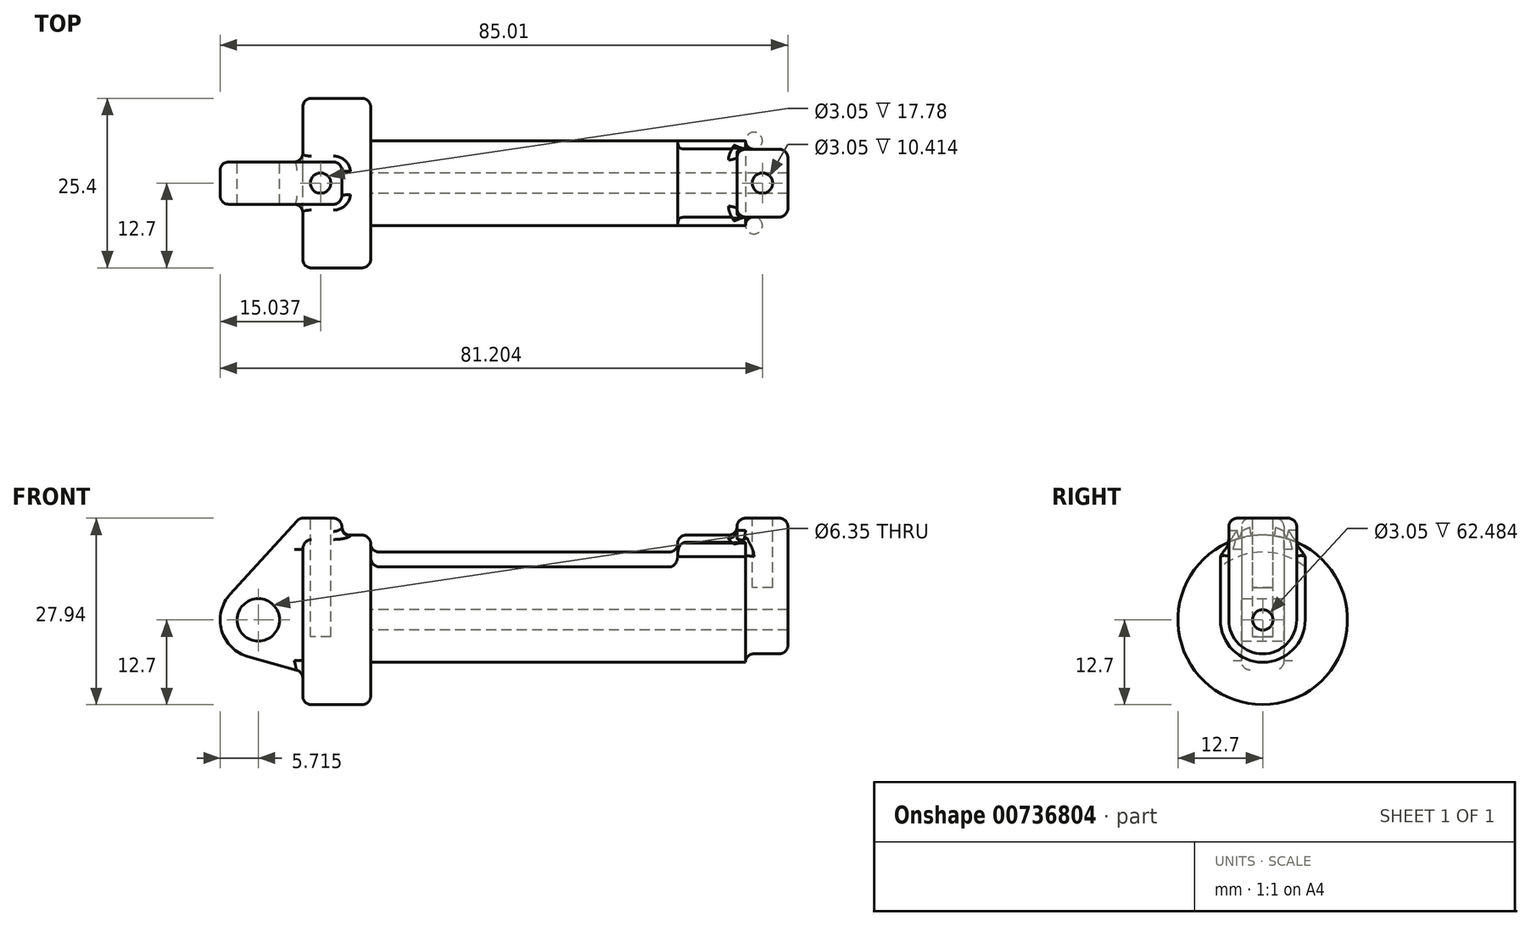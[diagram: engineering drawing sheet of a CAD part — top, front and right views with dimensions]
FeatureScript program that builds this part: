
annotation { "Feature Type Name" : "Feature", "Feature Type Description" : "" }
export const myFeature = defineFeature(function(context is Context, id is Id, definition is map)
    precondition{}
    {
        {
            var Q0;
            Q0=qCreatedBy(makeId("Front.planeOp"),FACE);
            var sketch = newSketch(context, id + "F0", { "sketchPlane" : qUnion([Q0])});
            skLineSegment(sketch, "E0", {"start": v(0, 0) * mm, "end": v(0, 12.7) * mm});
            skLineSegment(sketch, "E1", {"start": v(0, 12.7) * mm, "end": v(10.16, 12.7) * mm});
            skLineSegment(sketch, "E2", {"start": v(10.16, 12.7) * mm, "end": v(10.16, 10.16) * mm});
            skLineSegment(sketch, "E3", {"start": v(10.16, 10.16) * mm, "end": v(56.13, 10.16) * mm});
            skLineSegment(sketch, "E4", {"start": v(56.13, 10.16) * mm, "end": v(56.13, 12.7) * mm});
            skLineSegment(sketch, "E5", {"start": v(56.13, 12.7) * mm, "end": v(66.3, 12.7) * mm});
            skLineSegment(sketch, "E6", {"start": v(66.3, 12.7) * mm, "end": v(66.3, 0) * mm});
            skLineSegment(sketch, "E7", {"start": v(66.3, 0) * mm, "end": v(0, 0) * mm});
            skLineSegment(sketch, "E8", {"start": v(5.84, 15.24) * mm, "end": v(-0.5, 15.24) * mm});
            skLineSegment(sketch, "E9", {"start": v(-0.5, 15.24) * mm, "end": v(-10.88, 3.85) * mm});
            skLineSegment(sketch, "E10", {"start": v(0, 0) * mm, "end": v(-6.65, 0) * mm});
            skCircle(sketch, "E11", {"center": v(-6.65, 0) * mm, "radius": 5.72 * mm});
            skCircle(sketch, "E12", {"center": v(-6.65, 0) * mm, "radius": 3.18 * mm});
            skLineSegment(sketch, "E13", {"start": v(5.84, 15.24) * mm, "end": v(5.84, -9.4) * mm});
            skLineSegment(sketch, "E14", {"start": v(5.84, -9.4) * mm, "end": v(-8.18, -5.5) * mm});
            skSolve(sketch);
        }
        {
            var Q0;
            {var subQ0=sQuery(id+"F0.wireOp",EDGE,"E2");Q0=makeQuery(id+"F0.imprint","IMPRINT",FACE,{"disambiguationData":[TD([[makeQuery(id+"F0.imprint","IMPRINT",EDGE,{"derivedFrom":subQ0}),-1.0]])]});}
            var Q1;
            {var subQ0=sQuery(id+"F0.wireOp",EDGE,"E0");Q1=makeQuery(id+"F0.imprint","IMPRINT",FACE,{"disambiguationData":[TD([[makeQuery(id+"F0.imprint","IMPRINT",EDGE,{"derivedFrom":subQ0}),-1.0]])]});}
            var Q2;
            Q2=sQuery(id+"F0.wireOp",EDGE,"E7");
            revolve(context, id + "F1", {"surfaceOperationType" : NewSurfaceOperationType.NEW, "entities" : qUnion([Q0, Q1]), "axis" : qUnion([Q2]), "revolveType" : RevolveType.FULL});
        }
        {
            var Q0;
            {var subQ1=sQuery(id+"F0.wireOp",EDGE,"E0");Q0=makeQuery(id+"F0.imprint","IMPRINT",FACE,{"disambiguationData":[TD([[makeQuery(id+"F0.imprint","IMPRINT",EDGE,{"derivedFrom":subQ1}),1.0]])]});}
            var Q1;
            {var subQ0=sQuery(id+"F0.wireOp",EDGE,"E0");Q1=makeQuery(id+"F0.imprint","IMPRINT",FACE,{"disambiguationData":[TD([[makeQuery(id+"F0.imprint","IMPRINT",EDGE,{"derivedFrom":subQ0}),-1.0]])]});}
            var Q2;
            {var subQ5=sQuery(id+"F0.wireOp",EDGE,"E12");Q2=makeQuery(id+"F0.imprint","IMPRINT",FACE,{"disambiguationData":[TD([[makeQuery(id+"F0.imprint","IMPRINT",EDGE,{"derivedFrom":subQ5}),-1.0]])]});}
            var Q3;
            {var subQ0=sQuery(id+"F0.wireOp",EDGE,"E14");Q3=makeQuery(id+"F0.imprint","IMPRINT",FACE,{"disambiguationData":[TD([[makeQuery(id+"F0.imprint","IMPRINT",EDGE,{"derivedFrom":subQ0}),-1.0]])]});}
            var Q4;
            Q4 = qSketchRegion(id + "F3", true);
            extrude(context, id + "F2", {"entities" : qUnion([Q0, Q1, Q2, Q3, Q4]), "operationType" : NewBodyOperationType.ADD, "endBound" : BoundingType.SYMMETRIC, "depth" : 6.35 * mm, "offsetDistance" : 25.4 * mm});
        }
        {
            var Q0;
            Q0=makeQuery(id+"F1.opRevolve","SWEPT_FACE",FACE,{"disambiguationData":[OSD([sQuery(id+"F0.wireOp",EDGE,"E6")])]});
            var sketch = newSketch(context, id + "F3", { "sketchPlane" : qUnion([Q0])});
            skCircle(sketch, "E15", {"center": v(0, 0) * mm, "radius": 1.52 * mm});
            skCircle(sketch, "E16", {"center": v(0, 0) * mm, "radius": 5.08 * mm});
            skLineSegment(sketch, "E17", {"start": v(5.08, 0) * mm, "end": v(5.08, 15.24) * mm});
            skLineSegment(sketch, "E18", {"start": v(-5.08, 0) * mm, "end": v(-5.08, 15.24) * mm});
            skArc(sketch, "E19.0.0", {"start": v(-3.17, 12.3) * mm, "mid": v(0, 12.7) * mm, "end": v(3.17, 12.3) * mm});
            skLineSegment(sketch, "E19.0.1", {"start": v(3.18, 12.3) * mm, "end": v(3.18, 15.24) * mm});
            skLineSegment(sketch, "E19.0.2", {"start": v(3.17, 15.24) * mm, "end": v(-3.18, 15.24) * mm});
            skLineSegment(sketch, "E19.0.3", {"start": v(-3.18, 15.24) * mm, "end": v(-3.18, 12.3) * mm});
            skLineSegment(sketch, "E20", {"start": v(3.18, 15.24) * mm, "end": v(5.08, 15.24) * mm});
            skLineSegment(sketch, "E21", {"start": v(-5.08, 15.24) * mm, "end": v(-3.18, 15.24) * mm});
            skSolve(sketch);
        }
        {
            var Q0;
            Q0=makeQuery(id+"F3.imprint","IMPRINT",FACE,{"disambiguationData":[TD([[makeQuery(id+"F3.imprint","IMPRINT",EDGE,{"derivedFrom":sQuery(id+"F3.wireOp",EDGE,"E15")}),-1.0]])]});
            var Q1;
            {var subQ0=sQuery(id+"F3.wireOp",EDGE,"E19.0.0");Q1=makeQuery(id+"F3.imprint","IMPRINT",FACE,{"disambiguationData":[TD([[makeQuery(id+"F3.imprint","IMPRINT",EDGE,{"derivedFrom":subQ0}),1.0]])]});}
            var Q2;
            {var subQ4=sQuery(id+"F3.wireOp",EDGE,"E19.0.3");Q2=makeQuery(id+"F3.imprint","IMPRINT",FACE,{"disambiguationData":[TD([[makeQuery(id+"F3.imprint","IMPRINT",EDGE,{"derivedFrom":subQ4}),-1.0]])]});}
            var Q3;
            Q3=makeQuery(id+"F3.imprint","IMPRINT",FACE,{"disambiguationData":[TD([[makeQuery(id+"F3.imprint","IMPRINT",EDGE,{"derivedFrom":sQuery(id+"F3.wireOp",EDGE,"E19.0.0")}),-1.0]])]});
            var Q4;
            {var subQ4=sQuery(id+"F3.wireOp",EDGE,"E19.0.1");Q4=makeQuery(id+"F3.imprint","IMPRINT",FACE,{"disambiguationData":[TD([[makeQuery(id+"F3.imprint","IMPRINT",EDGE,{"derivedFrom":subQ4}),-1.0]])]});}
            extrude(context, id + "F4", {"entities" : qUnion([Q0, Q1, Q2, Q3, Q4]), "operationType" : NewBodyOperationType.ADD, "depth" : 6.35 * mm, "offsetDistance" : 25.4 * mm, "hasSecondDirection" : true, "secondDirectionOppositeDirection" : true, "secondDirectionDepth" : 1.27 * mm});
        }
        {
            var Q0;
            Q0=makeQuery(id+"F4.boolean.opBoolean","SPLIT",FACE,{"disambiguationData":[TD([makeQuery(id+"F4.opExtrude","SWEPT_FACE",FACE,{"disambiguationData":[OSD([sQuery(id+"F3.wireOp",EDGE,"E15")])]})])],"derivedFrom":makeQuery(id+"F1.opRevolve","SWEPT_FACE",FACE,{"disambiguationData":[OSD([sQuery(id+"F0.wireOp",EDGE,"E6")])]})});
            var Q1;
            Q1=makeQuery(id+"F1.opRevolve","SWEPT_FACE",FACE,{"disambiguationData":[OSD([sQuery(id+"F0.wireOp",EDGE,"E2")])]});
            extrude(context, id + "F5", {"entities" : qUnion([Q0]), "operationType" : NewBodyOperationType.REMOVE, "endBound" : BoundingType.UP_TO_SURFACE, "oppositeDirection" : true, "depth" : 25.4 * mm, "endBoundEntityFace" : qUnion([Q1]), "offsetDistance" : 25.4 * mm});
        }
        {
            var Q0;
            Q0=makeQuery(id+"F4.opExtrude","SWEPT_FACE",FACE,{"disambiguationData":[OSD([sQuery(id+"F3.wireOp",EDGE,"E19.0.2"),sQuery(id+"F3.wireOp",EDGE,"E20"),sQuery(id+"F3.wireOp",EDGE,"E21")])]});
            var sketch = newSketch(context, id + "F6", { "sketchPlane" : qUnion([Q0])});
            skLineSegment(sketch, "E22.0.0", {"start": v(5.84, 3.18) * mm, "end": v(-0.5, 3.18) * mm});
            skLineSegment(sketch, "E22.0.1", {"start": v(-0.5, 3.17) * mm, "end": v(-0.5, -3.18) * mm});
            skLineSegment(sketch, "E22.0.2", {"start": v(-0.5, -3.18) * mm, "end": v(5.84, -3.18) * mm});
            skLineSegment(sketch, "E22.0.3", {"start": v(5.84, -3.18) * mm, "end": v(5.84, 3.17) * mm});
            skPoint(sketch, "E23.0", {"position": v(2.67, 0) * mm});
            skCircle(sketch, "E24", {"center": v(2.67, 0) * mm, "radius": 1.52 * mm});
            skLineSegment(sketch, "E25", {"start": v(68.83, -5.08) * mm, "end": v(68.83, 5.08) * mm, "construction": true});
            skLineSegment(sketch, "E26", {"start": v(68.83, 5.08) * mm, "end": v(68.93, 5.05) * mm});
            skLineSegment(sketch, "E27", {"start": v(65.02, 0) * mm, "end": v(72.64, 0) * mm, "construction": true});
            skLineSegment(sketch, "E28", {"start": v(72.64, 0) * mm, "end": v(72.74, -0.13) * mm});
            skCircle(sketch, "E29", {"center": v(68.83, 0) * mm, "radius": 1.52 * mm});
            skSolve(sketch);
        }
        {
            var Q0;
            Q0=makeQuery(id+"F6.imprint","IMPRINT",FACE,{"disambiguationData":[TD([[makeQuery(id+"F6.imprint","IMPRINT",EDGE,{"derivedFrom":sQuery(id+"F6.wireOp",EDGE,"E24")}),1.0]])]});
            extrude(context, id + "F7", {"entities" : qUnion([Q0]), "operationType" : NewBodyOperationType.REMOVE, "oppositeDirection" : true, "depth" : 17.78 * mm, "offsetDistance" : 25.4 * mm});
        }
        {
            var Q0;
            Q0=makeQuery(id+"F6.imprint","IMPRINT",FACE,{"disambiguationData":[TD([[makeQuery(id+"F6.imprint","IMPRINT",EDGE,{"derivedFrom":sQuery(id+"F6.wireOp",EDGE,"E29")}),1.0]])]});
            var Q1;
            Q1=sQuery(id+"F6.wireOp",EDGE,"E29");
            extrude(context, id + "F8", {"entities" : qUnion([Q0]), "operationType" : NewBodyOperationType.REMOVE, "surfaceEntities" : qUnion([Q1]), "oppositeDirection" : true, "depth" : 10.4 * mm, "offsetDistance" : 25.4 * mm});
        }
        {
            var Q0;
            Q0=makeQuery(id+"F4.opExtrude","CAP_EDGE",EDGE,{"disambiguationData":[OSD([sQuery(id+"F3.wireOp",EDGE,"E19.0.2"),sQuery(id+"F3.wireOp",EDGE,"E20"),sQuery(id+"F3.wireOp",EDGE,"E21")])],"isStart":false});
            var Q1;
            Q1=makeQuery(id+"F1.opRevolve","SWEPT_EDGE",EDGE,{"disambiguationData":[OSD([sQuery(id+"F0.wireOp",EDGE,"E4"),sQuery(id+"F0.wireOp",EDGE,"E5")])]});
            var Q2;
            Q2=makeQuery(id+"F1.opRevolve","SWEPT_EDGE",EDGE,{"disambiguationData":[OSD([sQuery(id+"F0.wireOp",EDGE,"E1"),sQuery(id+"F0.wireOp",EDGE,"E2")])]});
            var Q3;
            Q3=makeQuery(id+"F1.opRevolve","SWEPT_EDGE",EDGE,{"disambiguationData":[OSD([sQuery(id+"F0.wireOp",EDGE,"E0"),sQuery(id+"F0.wireOp",EDGE,"E1")])]});
            var Q4;
            Q4=makeQuery(id+"F1.opRevolve","SWEPT_EDGE",EDGE,{"disambiguationData":[OSD([sQuery(id+"F0.wireOp",EDGE,"E5"),sQuery(id+"F0.wireOp",EDGE,"E6")])]});
            var Q5;
            Q5=makeQuery(id+"F4.opExtrude","CAP_EDGE",EDGE,{"disambiguationData":[OSD([sQuery(id+"F3.wireOp",EDGE,"E18")])],"isStart":false});
            var Q6;
            Q6=makeQuery(id+"F4.opExtrude","CAP_EDGE",EDGE,{"disambiguationData":[OSD([sQuery(id+"F3.wireOp",EDGE,"E17")])],"isStart":false});
            var Q7;
            Q7=makeQuery(id+"F4.opExtrude","CAP_EDGE",EDGE,{"disambiguationData":[OSD([sQuery(id+"F3.wireOp",EDGE,"E16")])],"isStart":false});
            var Q8;
            Q8=makeQuery(id+"F4.opExtrude","SWEPT_EDGE",EDGE,{"disambiguationData":[OSD([sQuery(id+"F3.wireOp",EDGE,"E17"),sQuery(id+"F3.wireOp",EDGE,"E20")])]});
            var Q9;
            Q9=makeQuery(id+"F1.opRevolve","SWEPT_EDGE",EDGE,{"disambiguationData":[OSD([sQuery(id+"F0.wireOp",EDGE,"E2"),sQuery(id+"F0.wireOp",EDGE,"E3")])]});
            var Q10;
            Q10=makeQuery(id+"F4.boolean.opBoolean","INTERSECT",EDGE,{"derivedFrom":[makeQuery(id+"F1.opRevolve","SWEPT_FACE",FACE,{"disambiguationData":[OSD([sQuery(id+"F0.wireOp",EDGE,"E6")])]}),makeQuery(id+"F4.opExtrude","SWEPT_FACE",FACE,{"disambiguationData":[OSD([sQuery(id+"F3.wireOp",EDGE,"E17")])]})]});
            var Q11;
            Q11=makeQuery(id+"F2.opExtrude","CAP_EDGE",EDGE,{"disambiguationData":[OSD([sQuery(id+"F0.wireOp",EDGE,"E8")])],"isStart":true});
            var Q12;
            Q12=makeQuery(id+"F2.opExtrude","SWEPT_EDGE",EDGE,{"disambiguationData":[OSD([sQuery(id+"F0.wireOp",EDGE,"E8"),sQuery(id+"F0.wireOp",EDGE,"E13")])]});
            var Q13;
            Q13=makeQuery(id+"F2.opExtrude","CAP_EDGE",EDGE,{"disambiguationData":[OSD([sQuery(id+"F0.wireOp",EDGE,"E11")])],"isStart":true});
            var Q14;
            Q14=makeQuery(id+"F2.opExtrude","CAP_EDGE",EDGE,{"disambiguationData":[OSD([sQuery(id+"F0.wireOp",EDGE,"E9")])],"isStart":true});
            var Q15;
            Q15=makeQuery(id+"F2.opExtrude","CAP_EDGE",EDGE,{"disambiguationData":[OSD([sQuery(id+"F0.wireOp",EDGE,"E13")])],"isStart":false});
            var Q16;
            Q16=makeQuery(id+"F2.boolean.opBoolean","INTERSECT",EDGE,{"derivedFrom":[makeQuery(id+"F1.opRevolve","SWEPT_FACE",FACE,{"disambiguationData":[OSD([sQuery(id+"F0.wireOp",EDGE,"E0")])]}),makeQuery(id+"F2.opExtrude","CAP_FACE",FACE,{"disambiguationData":[OSD([sQuery(id+"F0.wireOp",EDGE,"E8"),sQuery(id+"F0.wireOp",EDGE,"E9"),sQuery(id+"F0.wireOp",EDGE,"E11"),sQuery(id+"F0.wireOp",EDGE,"E12"),sQuery(id+"F0.wireOp",EDGE,"E13"),sQuery(id+"F0.wireOp",EDGE,"E14")])],"isStart":false})]});
            var Q17;
            Q17=makeQuery(id+"F2.opExtrude","CAP_EDGE",EDGE,{"disambiguationData":[OSD([sQuery(id+"F0.wireOp",EDGE,"E8")])],"isStart":false});
            var Q18;
            Q18=makeQuery(id+"F1.opRevolve","SWEPT_EDGE",EDGE,{"disambiguationData":[OSD([sQuery(id+"F0.wireOp",EDGE,"E3"),sQuery(id+"F0.wireOp",EDGE,"E4")])]});
            var Q19;
            Q19=makeQuery(id+"F2.opExtrude","CAP_EDGE",EDGE,{"disambiguationData":[OSD([sQuery(id+"F0.wireOp",EDGE,"E14")])],"isStart":true});
            var Q20;
            Q20=makeQuery(id+"F2.boolean.opBoolean","INTERSECT",EDGE,{"derivedFrom":[makeQuery(id+"F1.opRevolve","SWEPT_FACE",FACE,{"disambiguationData":[OSD([sQuery(id+"F0.wireOp",EDGE,"E1")])]}),makeQuery(id+"F2.opExtrude","SWEPT_FACE",FACE,{"disambiguationData":[OSD([sQuery(id+"F0.wireOp",EDGE,"E13")])]})]});
            var Q21;
            Q21=makeQuery(id+"F4.opExtrude","SWEPT_EDGE",EDGE,{"disambiguationData":[OSD([sQuery(id+"F3.wireOp",EDGE,"E18"),sQuery(id+"F3.wireOp",EDGE,"E21")])]});
            var Q22;
            Q22=makeQuery(id+"F4.opExtrude","CAP_EDGE",EDGE,{"disambiguationData":[OSD([sQuery(id+"F3.wireOp",EDGE,"E17")])],"isStart":true});
            var Q23;
            Q23=makeQuery(id+"F4.opExtrude","SWEPT_EDGE",EDGE,{"disambiguationData":[OSD([sQuery(id+"F3.wireOp",EDGE,"E16"),sQuery(id+"F3.wireOp",EDGE,"E17")])]});
            var Q24;
            Q24=makeQuery(id+"F4.opExtrude","CAP_EDGE",EDGE,{"disambiguationData":[OSD([sQuery(id+"F3.wireOp",EDGE,"E19.0.2"),sQuery(id+"F3.wireOp",EDGE,"E20"),sQuery(id+"F3.wireOp",EDGE,"E21")])],"isStart":true});
            var Q25;
            Q25=makeQuery(id+"F2.boolean.opBoolean","INTERSECT",EDGE,{"derivedFrom":[makeQuery(id+"F1.opRevolve","SWEPT_FACE",FACE,{"disambiguationData":[OSD([sQuery(id+"F0.wireOp",EDGE,"E1")])]}),makeQuery(id+"F2.opExtrude","CAP_FACE",FACE,{"disambiguationData":[OSD([sQuery(id+"F0.wireOp",EDGE,"E8"),sQuery(id+"F0.wireOp",EDGE,"E9"),sQuery(id+"F0.wireOp",EDGE,"E11"),sQuery(id+"F0.wireOp",EDGE,"E12"),sQuery(id+"F0.wireOp",EDGE,"E13"),sQuery(id+"F0.wireOp",EDGE,"E14")])],"isStart":true})]});
            var Q26;
            Q26=makeQuery(id+"F4.boolean.opBoolean","INTERSECT",EDGE,{"derivedFrom":[makeQuery(id+"F1.opRevolve","SWEPT_FACE",FACE,{"disambiguationData":[OSD([sQuery(id+"F0.wireOp",EDGE,"E5")])]}),makeQuery(id+"F4.opExtrude","CAP_FACE",FACE,{"disambiguationData":[OSD([sQuery(id+"F3.wireOp",EDGE,"E15"),sQuery(id+"F3.wireOp",EDGE,"E16"),sQuery(id+"F3.wireOp",EDGE,"E17"),sQuery(id+"F3.wireOp",EDGE,"E18"),sQuery(id+"F3.wireOp",EDGE,"E19.0.2"),sQuery(id+"F3.wireOp",EDGE,"E20"),sQuery(id+"F3.wireOp",EDGE,"E21")])],"isStart":true})]});
            var Q27;
            Q27=makeQuery(id+"F4.boolean.opBoolean","INTERSECT",EDGE,{"derivedFrom":[makeQuery(id+"F1.opRevolve","SWEPT_FACE",FACE,{"disambiguationData":[OSD([sQuery(id+"F0.wireOp",EDGE,"E6")])]}),makeQuery(id+"F4.opExtrude","SWEPT_FACE",FACE,{"disambiguationData":[OSD([sQuery(id+"F3.wireOp",EDGE,"E16")])]})]});
            var Q28;
            Q28=makeQuery(id+"F4.boolean.opBoolean","INTERSECT",EDGE,{"derivedFrom":[makeQuery(id+"F1.opRevolve","SWEPT_FACE",FACE,{"disambiguationData":[OSD([sQuery(id+"F0.wireOp",EDGE,"E6")])]}),makeQuery(id+"F4.opExtrude","SWEPT_FACE",FACE,{"disambiguationData":[OSD([sQuery(id+"F3.wireOp",EDGE,"E18")])]})]});
            var Q29;
            Q29=makeQuery(id+"F2.opExtrude","SWEPT_EDGE",EDGE,{"disambiguationData":[OSD([sQuery(id+"F0.wireOp",EDGE,"E8"),sQuery(id+"F0.wireOp",EDGE,"E9")])]});
            var Q30;
            Q30=makeQuery(id+"F2.boolean.opBoolean","INTERSECT",EDGE,{"derivedFrom":[makeQuery(id+"F1.opRevolve","SWEPT_FACE",FACE,{"disambiguationData":[OSD([sQuery(id+"F0.wireOp",EDGE,"E1")])]}),makeQuery(id+"F2.opExtrude","CAP_FACE",FACE,{"disambiguationData":[OSD([sQuery(id+"F0.wireOp",EDGE,"E8"),sQuery(id+"F0.wireOp",EDGE,"E9"),sQuery(id+"F0.wireOp",EDGE,"E11"),sQuery(id+"F0.wireOp",EDGE,"E12"),sQuery(id+"F0.wireOp",EDGE,"E13"),sQuery(id+"F0.wireOp",EDGE,"E14")])],"isStart":false})]});
            var Q31;
            Q31=makeQuery(id+"F2.boolean.opBoolean","INTERSECT",EDGE,{"derivedFrom":[makeQuery(id+"F1.opRevolve","SWEPT_FACE",FACE,{"disambiguationData":[OSD([sQuery(id+"F0.wireOp",EDGE,"E0")])]}),makeQuery(id+"F2.opExtrude","CAP_FACE",FACE,{"disambiguationData":[OSD([sQuery(id+"F0.wireOp",EDGE,"E8"),sQuery(id+"F0.wireOp",EDGE,"E9"),sQuery(id+"F0.wireOp",EDGE,"E11"),sQuery(id+"F0.wireOp",EDGE,"E12"),sQuery(id+"F0.wireOp",EDGE,"E13"),sQuery(id+"F0.wireOp",EDGE,"E14")])],"isStart":true})]});
            var Q32;
            Q32=makeQuery(id+"F2.opExtrude","CAP_EDGE",EDGE,{"disambiguationData":[OSD([sQuery(id+"F0.wireOp",EDGE,"E13")])],"isStart":true});
            var Q33;
            Q33=makeQuery(id+"F2.opExtrude","CAP_EDGE",EDGE,{"disambiguationData":[OSD([sQuery(id+"F0.wireOp",EDGE,"E14")])],"isStart":false});
            var Q34;
            Q34=makeQuery(id+"F4.opExtrude","CAP_EDGE",EDGE,{"disambiguationData":[OSD([sQuery(id+"F3.wireOp",EDGE,"E18")])],"isStart":true});
            var Q35;
            Q35=makeQuery(id+"F2.opExtrude","CAP_EDGE",EDGE,{"disambiguationData":[OSD([sQuery(id+"F0.wireOp",EDGE,"E11")])],"isStart":false});
            var Q36;
            Q36=makeQuery(id+"F2.boolean.opBoolean","INTERSECT",EDGE,{"derivedFrom":[makeQuery(id+"F1.opRevolve","SWEPT_FACE",FACE,{"disambiguationData":[OSD([sQuery(id+"F0.wireOp",EDGE,"E0")])]}),makeQuery(id+"F2.opExtrude","SWEPT_FACE",FACE,{"disambiguationData":[OSD([sQuery(id+"F0.wireOp",EDGE,"E14")])]})]});
            var Q37;
            Q37=makeQuery(id+"F2.opExtrude","CAP_EDGE",EDGE,{"disambiguationData":[OSD([sQuery(id+"F0.wireOp",EDGE,"E9")])],"isStart":false});
            var Q38;
            Q38=makeQuery(id+"F2.opExtrude","SWEPT_EDGE",EDGE,{"disambiguationData":[OSD([sQuery(id+"F0.wireOp",EDGE,"E9"),sQuery(id+"F0.wireOp",EDGE,"E11")])]});
            var Q39;
            Q39=makeQuery(id+"F2.opExtrude","SWEPT_EDGE",EDGE,{"disambiguationData":[OSD([sQuery(id+"F0.wireOp",EDGE,"E11"),sQuery(id+"F0.wireOp",EDGE,"E14")])]});
            var Q40;
            Q40=makeQuery(id+"F4.opExtrude","SWEPT_EDGE",EDGE,{"disambiguationData":[OSD([sQuery(id+"F3.wireOp",EDGE,"E16"),sQuery(id+"F3.wireOp",EDGE,"E18")])]});
            var Q41;
            Q41=makeQuery(id+"F4.boolean.opBoolean","INTERSECT",EDGE,{"derivedFrom":[makeQuery(id+"F1.opRevolve","SWEPT_FACE",FACE,{"disambiguationData":[OSD([sQuery(id+"F0.wireOp",EDGE,"E5")])]}),makeQuery(id+"F4.opExtrude","SWEPT_FACE",FACE,{"disambiguationData":[OSD([sQuery(id+"F3.wireOp",EDGE,"E17")])]})]});
            var Q42;
            Q42=makeQuery(id+"F4.boolean.opBoolean","INTERSECT",EDGE,{"derivedFrom":[makeQuery(id+"F1.opRevolve","SWEPT_FACE",FACE,{"disambiguationData":[OSD([sQuery(id+"F0.wireOp",EDGE,"E5")])]}),makeQuery(id+"F4.opExtrude","SWEPT_FACE",FACE,{"disambiguationData":[OSD([sQuery(id+"F3.wireOp",EDGE,"E18")])]})]});
            fillet(context, id + "F9", {"entities" : qUnion([Q0, Q1, Q2, Q3, Q4, Q5, Q6, Q7, Q8, Q9, Q10, Q11, Q12, Q13, Q14, Q15, Q16, Q17, Q18, Q19, Q20, Q21, Q22, Q23, Q24, Q25, Q26, Q27, Q28, Q29, Q30, Q31, Q32, Q33, Q34, Q35, Q36, Q37, Q38, Q39, Q40, Q41, Q42]), "radius" : 1.27 * mm, "tangentPropagation" : true, "allowEdgeOverflow" : false});
        }
    });
